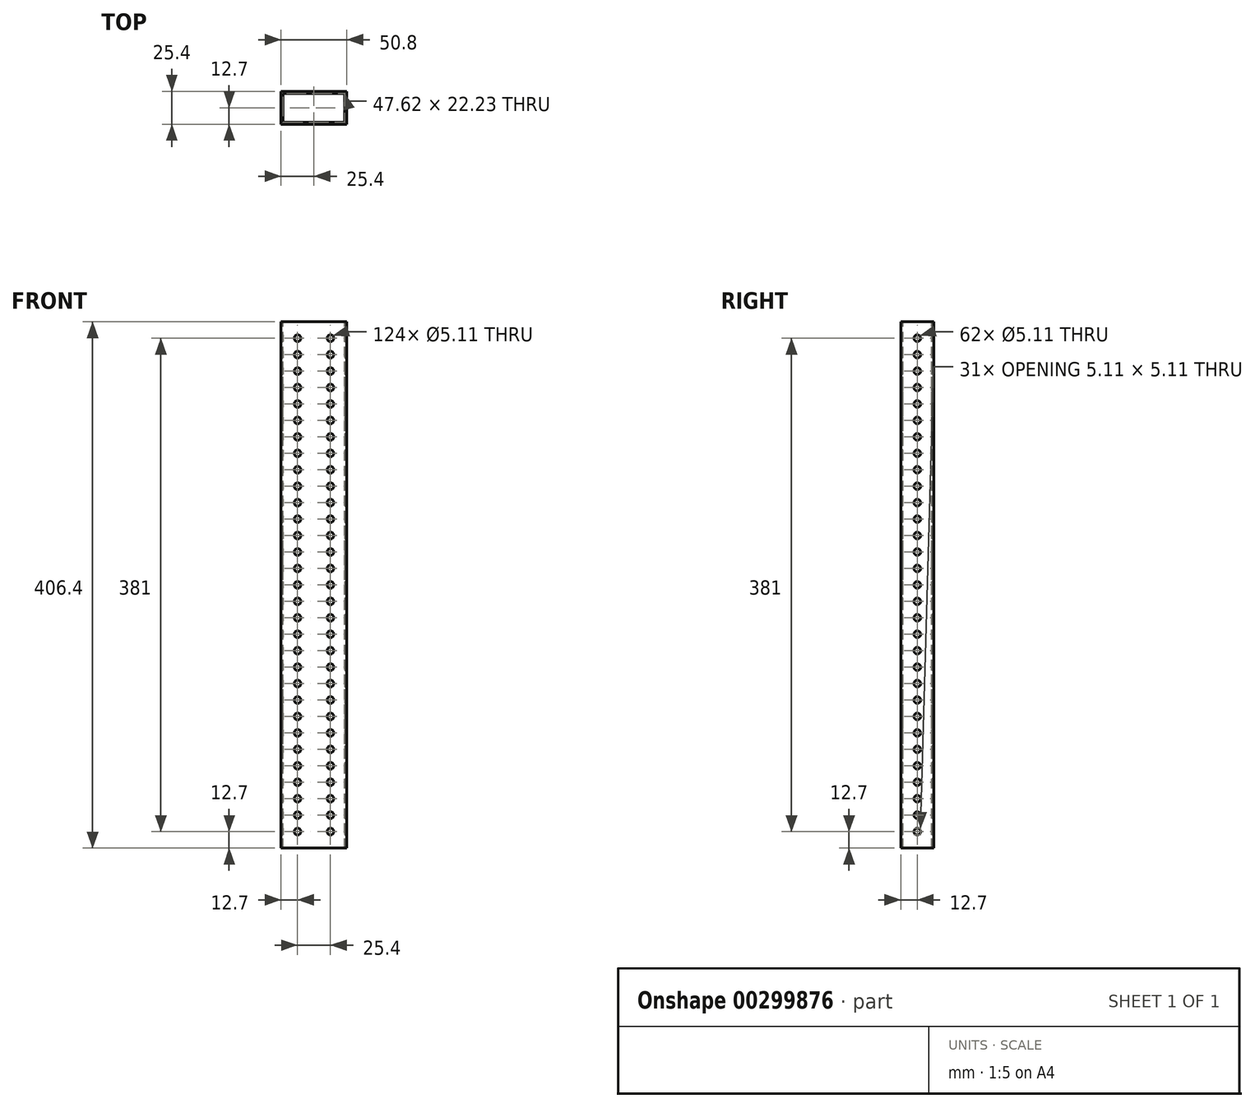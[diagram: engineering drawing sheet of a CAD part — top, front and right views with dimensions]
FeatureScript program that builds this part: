
annotation { "Feature Type Name" : "Feature", "Feature Type Description" : "" }
export const myFeature = defineFeature(function(context is Context, id is Id, definition is map)
    precondition{}
    {
        {
            var Q0;
            Q0=qCreatedBy(makeId("Top.planeOp"),FACE);
            var sketch = newSketch(context, id + "F0", { "sketchPlane" : qUnion([Q0])});
            skLineSegment(sketch, "E0.bottom", {"start": v(-25.4, 12.7) * mm, "end": v(25.4, 12.7) * mm});
            skLineSegment(sketch, "E0.top", {"start": v(-25.4, -12.7) * mm, "end": v(25.4, -12.7) * mm});
            skLineSegment(sketch, "E0.left", {"start": v(-25.4, 12.7) * mm, "end": v(-25.4, -12.7) * mm});
            skLineSegment(sketch, "E0.right", {"start": v(25.4, 12.7) * mm, "end": v(25.4, -12.7) * mm});
            skPoint(sketch, "E0.middle", {"position": v(0, 0) * mm});
            skSolve(sketch);
        }
        {
            var Q0;
            Q0=makeQuery(id+"F0.imprint","IMPRINT",FACE,{"disambiguationData":[TD([[makeQuery(id+"F0.imprint","IMPRINT",EDGE,{"derivedFrom":sQuery(id+"F0.wireOp",EDGE,"E0.bottom")}),-1.0]])]});
            extrude(context, id + "F1", {"entities" : qUnion([Q0]), "depth" : 406.4 * mm});
        }
        {
            var Q0;
            Q0=makeQuery(id+"F1.opExtrude","CAP_FACE",FACE,{"disambiguationData":[OSD([sQuery(id+"F0.wireOp",EDGE,"E0.bottom"),sQuery(id+"F0.wireOp",EDGE,"E0.top"),sQuery(id+"F0.wireOp",EDGE,"E0.left"),sQuery(id+"F0.wireOp",EDGE,"E0.right")])],"isStart":false});
            var sketch = newSketch(context, id + "F2", { "sketchPlane" : qUnion([Q0])});
            skLineSegment(sketch, "E1.bottom", {"start": v(-23.81, 11.11) * mm, "end": v(23.81, 11.11) * mm});
            skLineSegment(sketch, "E1.top", {"start": v(-23.81, -11.11) * mm, "end": v(23.81, -11.11) * mm});
            skLineSegment(sketch, "E1.left", {"start": v(-23.81, 11.11) * mm, "end": v(-23.81, -11.11) * mm});
            skLineSegment(sketch, "E1.right", {"start": v(23.81, 11.11) * mm, "end": v(23.81, -11.11) * mm});
            skPoint(sketch, "E1.middle", {"position": v(0, 0) * mm});
            skSolve(sketch);
        }
        {
            var Q0;
            Q0=makeQuery(id+"F2.imprint","IMPRINT",FACE,{"disambiguationData":[TD([[makeQuery(id+"F2.imprint","IMPRINT",EDGE,{"derivedFrom":sQuery(id+"F2.wireOp",EDGE,"E1.bottom")}),-1.0]])]});
            extrude(context, id + "F3", {"entities" : qUnion([Q0]), "operationType" : NewBodyOperationType.REMOVE, "oppositeDirection" : true, "depth" : 406.4 * mm});
        }
        {
            var Q0;
            Q0=makeQuery(id+"F1.opExtrude","SWEPT_FACE",FACE,{"disambiguationData":[OSD([sQuery(id+"F0.wireOp",EDGE,"E0.right")])]});
            var sketch = newSketch(context, id + "F4", { "sketchPlane" : qUnion([Q0])});
            skCircle(sketch, "E2", {"center": v(0, 12.7) * mm, "radius": 2.55 * mm});
            skCircle(sketch, "E3.0.1.0", {"center": v(0, 25.4) * mm, "radius": 2.55 * mm});
            skCircle(sketch, "E3.0.2.0", {"center": v(0, 38.1) * mm, "radius": 2.55 * mm});
            skCircle(sketch, "E3.0.3.0", {"center": v(0, 50.8) * mm, "radius": 2.55 * mm});
            skCircle(sketch, "E3.0.4.0", {"center": v(0, 63.5) * mm, "radius": 2.55 * mm});
            skCircle(sketch, "E3.0.5.0", {"center": v(0, 76.2) * mm, "radius": 2.55 * mm});
            skCircle(sketch, "E3.0.6.0", {"center": v(0, 88.9) * mm, "radius": 2.55 * mm});
            skCircle(sketch, "E3.0.7.0", {"center": v(0, 101.6) * mm, "radius": 2.55 * mm});
            skCircle(sketch, "E3.0.8.0", {"center": v(0, 114.3) * mm, "radius": 2.55 * mm});
            skCircle(sketch, "E3.0.9.0", {"center": v(0, 127) * mm, "radius": 2.55 * mm});
            skCircle(sketch, "E3.0.10.0", {"center": v(0, 139.7) * mm, "radius": 2.55 * mm});
            skCircle(sketch, "E3.0.11.0", {"center": v(0, 152.4) * mm, "radius": 2.55 * mm});
            skCircle(sketch, "E3.0.12.0", {"center": v(0, 165.1) * mm, "radius": 2.55 * mm});
            skCircle(sketch, "E3.0.13.0", {"center": v(0, 177.8) * mm, "radius": 2.55 * mm});
            skCircle(sketch, "E3.0.14.0", {"center": v(0, 190.5) * mm, "radius": 2.55 * mm});
            skCircle(sketch, "E3.0.15.0", {"center": v(0, 203.2) * mm, "radius": 2.55 * mm});
            skCircle(sketch, "E3.0.16.0", {"center": v(0, 215.9) * mm, "radius": 2.55 * mm});
            skCircle(sketch, "E3.0.17.0", {"center": v(0, 228.6) * mm, "radius": 2.55 * mm});
            skCircle(sketch, "E3.0.18.0", {"center": v(0, 241.3) * mm, "radius": 2.55 * mm});
            skCircle(sketch, "E3.0.19.0", {"center": v(0, 254) * mm, "radius": 2.55 * mm});
            skCircle(sketch, "E3.0.20.0", {"center": v(0, 266.7) * mm, "radius": 2.55 * mm});
            skCircle(sketch, "E3.0.21.0", {"center": v(0, 279.4) * mm, "radius": 2.55 * mm});
            skCircle(sketch, "E3.0.22.0", {"center": v(0, 292.1) * mm, "radius": 2.55 * mm});
            skCircle(sketch, "E3.0.23.0", {"center": v(0, 304.8) * mm, "radius": 2.55 * mm});
            skCircle(sketch, "E3.0.24.0", {"center": v(0, 317.5) * mm, "radius": 2.55 * mm});
            skCircle(sketch, "E3.0.25.0", {"center": v(0, 330.2) * mm, "radius": 2.55 * mm});
            skCircle(sketch, "E3.0.26.0", {"center": v(0, 342.9) * mm, "radius": 2.55 * mm});
            skCircle(sketch, "E3.0.27.0", {"center": v(0, 355.6) * mm, "radius": 2.55 * mm});
            skCircle(sketch, "E3.0.28.0", {"center": v(0, 368.3) * mm, "radius": 2.55 * mm});
            skCircle(sketch, "E3.0.29.0", {"center": v(0, 381) * mm, "radius": 2.55 * mm});
            skCircle(sketch, "E3.0.30.0", {"center": v(0, 393.7) * mm, "radius": 2.55 * mm});
            skLineSegment(sketch, "E3.direction1", {"start": v(0, 12.7) * mm, "end": v(25.4, 12.7) * mm, "construction": true});
            skLineSegment(sketch, "E3.direction2", {"start": v(0, 12.7) * mm, "end": v(0, 25.4) * mm, "construction": true});
            skSolve(sketch);
        }
        {
            var Q0;
            Q0=sQuery(id+"F4.wireOp",VERTEX,"E2.center");
            var Q1;
            Q1=sQuery(id+"F4.wireOp",VERTEX,"E3.0.1.0.center");
            var Q2;
            Q2=sQuery(id+"F4.wireOp",VERTEX,"E3.0.2.0.center");
            var Q3;
            Q3=sQuery(id+"F4.wireOp",VERTEX,"E3.0.21.0.center");
            var Q4;
            Q4=sQuery(id+"F4.wireOp",VERTEX,"E3.0.15.0.center");
            var Q5;
            Q5=sQuery(id+"F4.wireOp",VERTEX,"E3.0.22.0.center");
            var Q6;
            Q6=sQuery(id+"F4.wireOp",VERTEX,"E3.0.16.0.center");
            var Q7;
            Q7=sQuery(id+"F4.wireOp",VERTEX,"E3.0.25.0.center");
            var Q8;
            Q8=sQuery(id+"F4.wireOp",VERTEX,"E3.0.19.0.center");
            var Q9;
            Q9=sQuery(id+"F4.wireOp",VERTEX,"E3.0.12.0.center");
            var Q10;
            Q10=sQuery(id+"F4.wireOp",VERTEX,"E3.0.23.0.center");
            var Q11;
            Q11=sQuery(id+"F4.wireOp",VERTEX,"E3.0.17.0.center");
            var Q12;
            Q12=sQuery(id+"F4.wireOp",VERTEX,"E3.0.9.0.center");
            var Q13;
            Q13=sQuery(id+"F4.wireOp",VERTEX,"E3.0.10.0.center");
            var Q14;
            Q14=sQuery(id+"F4.wireOp",VERTEX,"E3.0.26.0.center");
            var Q15;
            Q15=sQuery(id+"F4.wireOp",VERTEX,"E3.0.11.0.center");
            var Q16;
            Q16=sQuery(id+"F4.wireOp",VERTEX,"E3.0.13.0.center");
            var Q17;
            Q17=sQuery(id+"F4.wireOp",VERTEX,"E3.0.3.0.center");
            var Q18;
            Q18=sQuery(id+"F4.wireOp",VERTEX,"E3.0.4.0.center");
            var Q19;
            Q19=sQuery(id+"F4.wireOp",VERTEX,"E3.0.5.0.center");
            var Q20;
            Q20=sQuery(id+"F4.wireOp",VERTEX,"E3.0.6.0.center");
            var Q21;
            Q21=sQuery(id+"F4.wireOp",VERTEX,"E3.0.7.0.center");
            var Q22;
            Q22=sQuery(id+"F4.wireOp",VERTEX,"E3.0.8.0.center");
            var Q23;
            Q23=sQuery(id+"F4.wireOp",VERTEX,"E3.0.24.0.center");
            var Q24;
            Q24=sQuery(id+"F4.wireOp",VERTEX,"E3.0.20.0.center");
            var Q25;
            Q25=sQuery(id+"F4.wireOp",VERTEX,"E3.0.18.0.center");
            var Q26;
            Q26=sQuery(id+"F4.wireOp",VERTEX,"E3.0.14.0.center");
            var Q27;
            Q27=sQuery(id+"F4.wireOp",VERTEX,"E3.0.28.0.center");
            var Q28;
            Q28=sQuery(id+"F4.wireOp",VERTEX,"E3.0.29.0.center");
            var Q29;
            Q29=sQuery(id+"F4.wireOp",VERTEX,"E3.0.27.0.center");
            var Q30;
            Q30=sQuery(id+"F4.wireOp",VERTEX,"E3.0.30.0.center");
            var Q31;
            Q31=makeQuery(id+"F1.opExtrude","SWEPT_BODY",BODY,{"disambiguationData":[OSD([sQuery(id+"F0.wireOp",EDGE,"E0.bottom"),sQuery(id+"F0.wireOp",EDGE,"E0.top"),sQuery(id+"F0.wireOp",EDGE,"E0.left"),sQuery(id+"F0.wireOp",EDGE,"E0.right")])]});
            hole(context, id + "F5", {"style" : HoleStyle.SIMPLE, "endStyle" : HoleEndStyle.THROUGH, "holeDiameter" : 5.1 * mm, "tappedDepth" : 12.7 * mm, "tapClearance" : 3, "locations" : qUnion([Q0, Q1, Q2, Q3, Q4, Q5, Q6, Q7, Q8, Q9, Q10, Q11, Q12, Q13, Q14, Q15, Q16, Q17, Q18, Q19, Q20, Q21, Q22, Q23, Q24, Q25, Q26, Q27, Q28, Q29, Q30]), "scope" : qUnion([Q31])});
        }
        {
            var Q0;
            Q0=makeQuery(id+"F1.opExtrude","SWEPT_FACE",FACE,{"disambiguationData":[OSD([sQuery(id+"F0.wireOp",EDGE,"E0.top")])]});
            var sketch = newSketch(context, id + "F6", { "sketchPlane" : qUnion([Q0])});
            skCircle(sketch, "E4", {"center": v(-12.7, 393.7) * mm, "radius": 2.55 * mm});
            skCircle(sketch, "E5.0.1.0", {"center": v(-12.7, 381) * mm, "radius": 2.55 * mm});
            skCircle(sketch, "E5.0.2.0", {"center": v(-12.7, 368.3) * mm, "radius": 2.55 * mm});
            skCircle(sketch, "E5.0.3.0", {"center": v(-12.7, 355.6) * mm, "radius": 2.55 * mm});
            skCircle(sketch, "E5.0.4.0", {"center": v(-12.7, 342.9) * mm, "radius": 2.55 * mm});
            skCircle(sketch, "E5.0.5.0", {"center": v(-12.7, 330.2) * mm, "radius": 2.55 * mm});
            skCircle(sketch, "E5.0.6.0", {"center": v(-12.7, 317.5) * mm, "radius": 2.55 * mm});
            skCircle(sketch, "E5.0.7.0", {"center": v(-12.7, 304.8) * mm, "radius": 2.55 * mm});
            skCircle(sketch, "E5.0.8.0", {"center": v(-12.7, 292.1) * mm, "radius": 2.55 * mm});
            skCircle(sketch, "E5.0.9.0", {"center": v(-12.7, 279.4) * mm, "radius": 2.55 * mm});
            skCircle(sketch, "E5.0.10.0", {"center": v(-12.7, 266.7) * mm, "radius": 2.55 * mm});
            skCircle(sketch, "E5.0.11.0", {"center": v(-12.7, 254) * mm, "radius": 2.55 * mm});
            skCircle(sketch, "E5.0.12.0", {"center": v(-12.7, 241.3) * mm, "radius": 2.55 * mm});
            skCircle(sketch, "E5.0.13.0", {"center": v(-12.7, 228.6) * mm, "radius": 2.55 * mm});
            skCircle(sketch, "E5.0.14.0", {"center": v(-12.7, 215.9) * mm, "radius": 2.55 * mm});
            skCircle(sketch, "E5.0.15.0", {"center": v(-12.7, 203.2) * mm, "radius": 2.55 * mm});
            skCircle(sketch, "E5.0.16.0", {"center": v(-12.7, 190.5) * mm, "radius": 2.55 * mm});
            skCircle(sketch, "E5.0.17.0", {"center": v(-12.7, 177.8) * mm, "radius": 2.55 * mm});
            skCircle(sketch, "E5.0.18.0", {"center": v(-12.7, 165.1) * mm, "radius": 2.55 * mm});
            skCircle(sketch, "E5.0.19.0", {"center": v(-12.7, 152.4) * mm, "radius": 2.55 * mm});
            skCircle(sketch, "E5.0.20.0", {"center": v(-12.7, 139.7) * mm, "radius": 2.55 * mm});
            skCircle(sketch, "E5.0.21.0", {"center": v(-12.7, 127) * mm, "radius": 2.55 * mm});
            skCircle(sketch, "E5.0.22.0", {"center": v(-12.7, 114.3) * mm, "radius": 2.55 * mm});
            skCircle(sketch, "E5.0.23.0", {"center": v(-12.7, 101.6) * mm, "radius": 2.55 * mm});
            skCircle(sketch, "E5.0.24.0", {"center": v(-12.7, 88.9) * mm, "radius": 2.55 * mm});
            skCircle(sketch, "E5.0.25.0", {"center": v(-12.7, 76.2) * mm, "radius": 2.55 * mm});
            skCircle(sketch, "E5.0.26.0", {"center": v(-12.7, 63.5) * mm, "radius": 2.55 * mm});
            skCircle(sketch, "E5.0.27.0", {"center": v(-12.7, 50.8) * mm, "radius": 2.55 * mm});
            skCircle(sketch, "E5.0.28.0", {"center": v(-12.7, 38.1) * mm, "radius": 2.55 * mm});
            skCircle(sketch, "E5.0.29.0", {"center": v(-12.7, 25.4) * mm, "radius": 2.55 * mm});
            skCircle(sketch, "E5.0.30.0", {"center": v(-12.7, 12.7) * mm, "radius": 2.55 * mm});
            skCircle(sketch, "E5.1.0.0", {"center": v(12.7, 393.7) * mm, "radius": 2.55 * mm});
            skCircle(sketch, "E5.1.1.0", {"center": v(12.7, 381) * mm, "radius": 2.55 * mm});
            skCircle(sketch, "E5.1.2.0", {"center": v(12.7, 368.3) * mm, "radius": 2.55 * mm});
            skCircle(sketch, "E5.1.3.0", {"center": v(12.7, 355.6) * mm, "radius": 2.55 * mm});
            skCircle(sketch, "E5.1.4.0", {"center": v(12.7, 342.9) * mm, "radius": 2.55 * mm});
            skCircle(sketch, "E5.1.5.0", {"center": v(12.7, 330.2) * mm, "radius": 2.55 * mm});
            skCircle(sketch, "E5.1.6.0", {"center": v(12.7, 317.5) * mm, "radius": 2.55 * mm});
            skCircle(sketch, "E5.1.7.0", {"center": v(12.7, 304.8) * mm, "radius": 2.55 * mm});
            skCircle(sketch, "E5.1.8.0", {"center": v(12.7, 292.1) * mm, "radius": 2.55 * mm});
            skCircle(sketch, "E5.1.9.0", {"center": v(12.7, 279.4) * mm, "radius": 2.55 * mm});
            skCircle(sketch, "E5.1.10.0", {"center": v(12.7, 266.7) * mm, "radius": 2.55 * mm});
            skCircle(sketch, "E5.1.11.0", {"center": v(12.7, 254) * mm, "radius": 2.55 * mm});
            skCircle(sketch, "E5.1.12.0", {"center": v(12.7, 241.3) * mm, "radius": 2.55 * mm});
            skCircle(sketch, "E5.1.13.0", {"center": v(12.7, 228.6) * mm, "radius": 2.55 * mm});
            skCircle(sketch, "E5.1.14.0", {"center": v(12.7, 215.9) * mm, "radius": 2.55 * mm});
            skCircle(sketch, "E5.1.15.0", {"center": v(12.7, 203.2) * mm, "radius": 2.55 * mm});
            skCircle(sketch, "E5.1.16.0", {"center": v(12.7, 190.5) * mm, "radius": 2.55 * mm});
            skCircle(sketch, "E5.1.17.0", {"center": v(12.7, 177.8) * mm, "radius": 2.55 * mm});
            skCircle(sketch, "E5.1.18.0", {"center": v(12.7, 165.1) * mm, "radius": 2.55 * mm});
            skCircle(sketch, "E5.1.19.0", {"center": v(12.7, 152.4) * mm, "radius": 2.55 * mm});
            skCircle(sketch, "E5.1.20.0", {"center": v(12.7, 139.7) * mm, "radius": 2.55 * mm});
            skCircle(sketch, "E5.1.21.0", {"center": v(12.7, 127) * mm, "radius": 2.55 * mm});
            skCircle(sketch, "E5.1.22.0", {"center": v(12.7, 114.3) * mm, "radius": 2.55 * mm});
            skCircle(sketch, "E5.1.23.0", {"center": v(12.7, 101.6) * mm, "radius": 2.55 * mm});
            skCircle(sketch, "E5.1.24.0", {"center": v(12.7, 88.9) * mm, "radius": 2.55 * mm});
            skCircle(sketch, "E5.1.25.0", {"center": v(12.7, 76.2) * mm, "radius": 2.55 * mm});
            skCircle(sketch, "E5.1.26.0", {"center": v(12.7, 63.5) * mm, "radius": 2.55 * mm});
            skCircle(sketch, "E5.1.27.0", {"center": v(12.7, 50.8) * mm, "radius": 2.55 * mm});
            skCircle(sketch, "E5.1.28.0", {"center": v(12.7, 38.1) * mm, "radius": 2.55 * mm});
            skCircle(sketch, "E5.1.29.0", {"center": v(12.7, 25.4) * mm, "radius": 2.55 * mm});
            skCircle(sketch, "E5.1.30.0", {"center": v(12.7, 12.7) * mm, "radius": 2.55 * mm});
            skLineSegment(sketch, "E5.direction1", {"start": v(-12.7, 393.7) * mm, "end": v(12.7, 393.7) * mm, "construction": true});
            skLineSegment(sketch, "E5.direction2", {"start": v(-12.7, 393.7) * mm, "end": v(-12.7, 381) * mm, "construction": true});
            skSolve(sketch);
        }
        {
            var Q0;
            Q0=sQuery(id+"F6.wireOp",VERTEX,"E5.1.14.0.center");
            var Q1;
            Q1=sQuery(id+"F6.wireOp",VERTEX,"E5.0.14.0.center");
            var Q2;
            Q2=sQuery(id+"F6.wireOp",VERTEX,"E5.0.3.0.center");
            var Q3;
            Q3=sQuery(id+"F6.wireOp",VERTEX,"E5.0.1.0.center");
            var Q4;
            Q4=sQuery(id+"F6.wireOp",VERTEX,"E5.0.2.0.center");
            var Q5;
            Q5=sQuery(id+"F6.wireOp",VERTEX,"E4.center");
            var Q6;
            Q6=sQuery(id+"F6.wireOp",VERTEX,"E5.direction1.end");
            var Q7;
            Q7=sQuery(id+"F6.wireOp",VERTEX,"E5.0.8.0.center");
            var Q8;
            Q8=sQuery(id+"F6.wireOp",VERTEX,"E5.0.6.0.center");
            var Q9;
            Q9=sQuery(id+"F6.wireOp",VERTEX,"E5.0.7.0.center");
            var Q10;
            Q10=sQuery(id+"F6.wireOp",VERTEX,"E5.0.4.0.center");
            var Q11;
            Q11=sQuery(id+"F6.wireOp",VERTEX,"E5.0.5.0.center");
            var Q12;
            Q12=sQuery(id+"F6.wireOp",VERTEX,"E5.0.11.0.center");
            var Q13;
            Q13=sQuery(id+"F6.wireOp",VERTEX,"E5.0.9.0.center");
            var Q14;
            Q14=sQuery(id+"F6.wireOp",VERTEX,"E5.0.10.0.center");
            var Q15;
            Q15=sQuery(id+"F6.wireOp",VERTEX,"E5.1.8.0.center");
            var Q16;
            Q16=sQuery(id+"F6.wireOp",VERTEX,"E5.1.24.0.center");
            var Q17;
            Q17=sQuery(id+"F6.wireOp",VERTEX,"E5.0.23.0.center");
            var Q18;
            Q18=sQuery(id+"F6.wireOp",VERTEX,"E5.0.17.0.center");
            var Q19;
            Q19=sQuery(id+"F6.wireOp",VERTEX,"E5.1.27.0.center");
            var Q20;
            Q20=sQuery(id+"F6.wireOp",VERTEX,"E5.0.26.0.center");
            var Q21;
            Q21=sQuery(id+"F6.wireOp",VERTEX,"E5.1.2.0.center");
            var Q22;
            Q22=sQuery(id+"F6.wireOp",VERTEX,"E5.1.11.0.center");
            var Q23;
            Q23=sQuery(id+"F6.wireOp",VERTEX,"E5.1.18.0.center");
            var Q24;
            Q24=sQuery(id+"F6.wireOp",VERTEX,"E5.1.9.0.center");
            var Q25;
            Q25=sQuery(id+"F6.wireOp",VERTEX,"E5.1.25.0.center");
            var Q26;
            Q26=sQuery(id+"F6.wireOp",VERTEX,"E5.0.24.0.center");
            var Q27;
            Q27=sQuery(id+"F6.wireOp",VERTEX,"E5.1.28.0.center");
            var Q28;
            Q28=sQuery(id+"F6.wireOp",VERTEX,"E5.1.19.0.center");
            var Q29;
            Q29=sQuery(id+"F6.wireOp",VERTEX,"E5.1.3.0.center");
            var Q30;
            Q30=sQuery(id+"F6.wireOp",VERTEX,"E5.0.27.0.center");
            var Q31;
            Q31=sQuery(id+"F6.wireOp",VERTEX,"E5.1.12.0.center");
            var Q32;
            Q32=sQuery(id+"F6.wireOp",VERTEX,"E5.0.18.0.center");
            var Q33;
            Q33=sQuery(id+"F6.wireOp",VERTEX,"E5.1.6.0.center");
            var Q34;
            Q34=sQuery(id+"F6.wireOp",VERTEX,"E5.1.22.0.center");
            var Q35;
            Q35=sQuery(id+"F6.wireOp",VERTEX,"E5.0.21.0.center");
            var Q36;
            Q36=sQuery(id+"F6.wireOp",VERTEX,"E5.0.30.0.center");
            var Q37;
            Q37=sQuery(id+"F6.wireOp",VERTEX,"E5.1.15.0.center");
            var Q38;
            Q38=sQuery(id+"F6.wireOp",VERTEX,"E5.0.15.0.center");
            var Q39;
            Q39=sQuery(id+"F6.wireOp",VERTEX,"E5.1.16.0.center");
            var Q40;
            Q40=sQuery(id+"F6.wireOp",VERTEX,"E5.1.7.0.center");
            var Q41;
            Q41=sQuery(id+"F6.wireOp",VERTEX,"E5.1.23.0.center");
            var Q42;
            Q42=sQuery(id+"F6.wireOp",VERTEX,"E5.0.22.0.center");
            var Q43;
            Q43=sQuery(id+"F6.wireOp",VERTEX,"E5.1.26.0.center");
            var Q44;
            Q44=sQuery(id+"F6.wireOp",VERTEX,"E5.1.1.0.center");
            var Q45;
            Q45=sQuery(id+"F6.wireOp",VERTEX,"E5.0.25.0.center");
            var Q46;
            Q46=sQuery(id+"F6.wireOp",VERTEX,"E5.1.17.0.center");
            var Q47;
            Q47=sQuery(id+"F6.wireOp",VERTEX,"E5.1.10.0.center");
            var Q48;
            Q48=sQuery(id+"F6.wireOp",VERTEX,"E5.0.16.0.center");
            var Q49;
            Q49=sQuery(id+"F6.wireOp",VERTEX,"E5.1.4.0.center");
            var Q50;
            Q50=sQuery(id+"F6.wireOp",VERTEX,"E5.1.20.0.center");
            var Q51;
            Q51=sQuery(id+"F6.wireOp",VERTEX,"E5.0.19.0.center");
            var Q52;
            Q52=sQuery(id+"F6.wireOp",VERTEX,"E5.1.29.0.center");
            var Q53;
            Q53=sQuery(id+"F6.wireOp",VERTEX,"E5.0.28.0.center");
            var Q54;
            Q54=sQuery(id+"F6.wireOp",VERTEX,"E5.1.13.0.center");
            var Q55;
            Q55=sQuery(id+"F6.wireOp",VERTEX,"E5.0.12.0.center");
            var Q56;
            Q56=sQuery(id+"F6.wireOp",VERTEX,"E5.1.5.0.center");
            var Q57;
            Q57=sQuery(id+"F6.wireOp",VERTEX,"E5.1.21.0.center");
            var Q58;
            Q58=sQuery(id+"F6.wireOp",VERTEX,"E5.0.20.0.center");
            var Q59;
            Q59=sQuery(id+"F6.wireOp",VERTEX,"E5.0.13.0.center");
            var Q60;
            Q60=sQuery(id+"F6.wireOp",VERTEX,"E5.1.30.0.center");
            var Q61;
            Q61=sQuery(id+"F6.wireOp",VERTEX,"E5.0.29.0.center");
            var Q62;
            Q62=makeQuery(id+"F1.opExtrude","SWEPT_BODY",BODY,{"disambiguationData":[OSD([sQuery(id+"F0.wireOp",EDGE,"E0.bottom"),sQuery(id+"F0.wireOp",EDGE,"E0.top"),sQuery(id+"F0.wireOp",EDGE,"E0.left"),sQuery(id+"F0.wireOp",EDGE,"E0.right")])]});
            hole(context, id + "F7", {"style" : HoleStyle.SIMPLE, "endStyle" : HoleEndStyle.THROUGH, "holeDiameter" : 5.1 * mm, "tappedDepth" : 12.7 * mm, "tapClearance" : 3, "locations" : qUnion([Q0, Q1, Q2, Q3, Q4, Q5, Q6, Q7, Q8, Q9, Q10, Q11, Q12, Q13, Q14, Q15, Q16, Q17, Q18, Q19, Q20, Q21, Q22, Q23, Q24, Q25, Q26, Q27, Q28, Q29, Q30, Q31, Q32, Q33, Q34, Q35, Q36, Q37, Q38, Q39, Q40, Q41, Q42, Q43, Q44, Q45, Q46, Q47, Q48, Q49, Q50, Q51, Q52, Q53, Q54, Q55, Q56, Q57, Q58, Q59, Q60, Q61]), "scope" : qUnion([Q62])});
        }
    });
